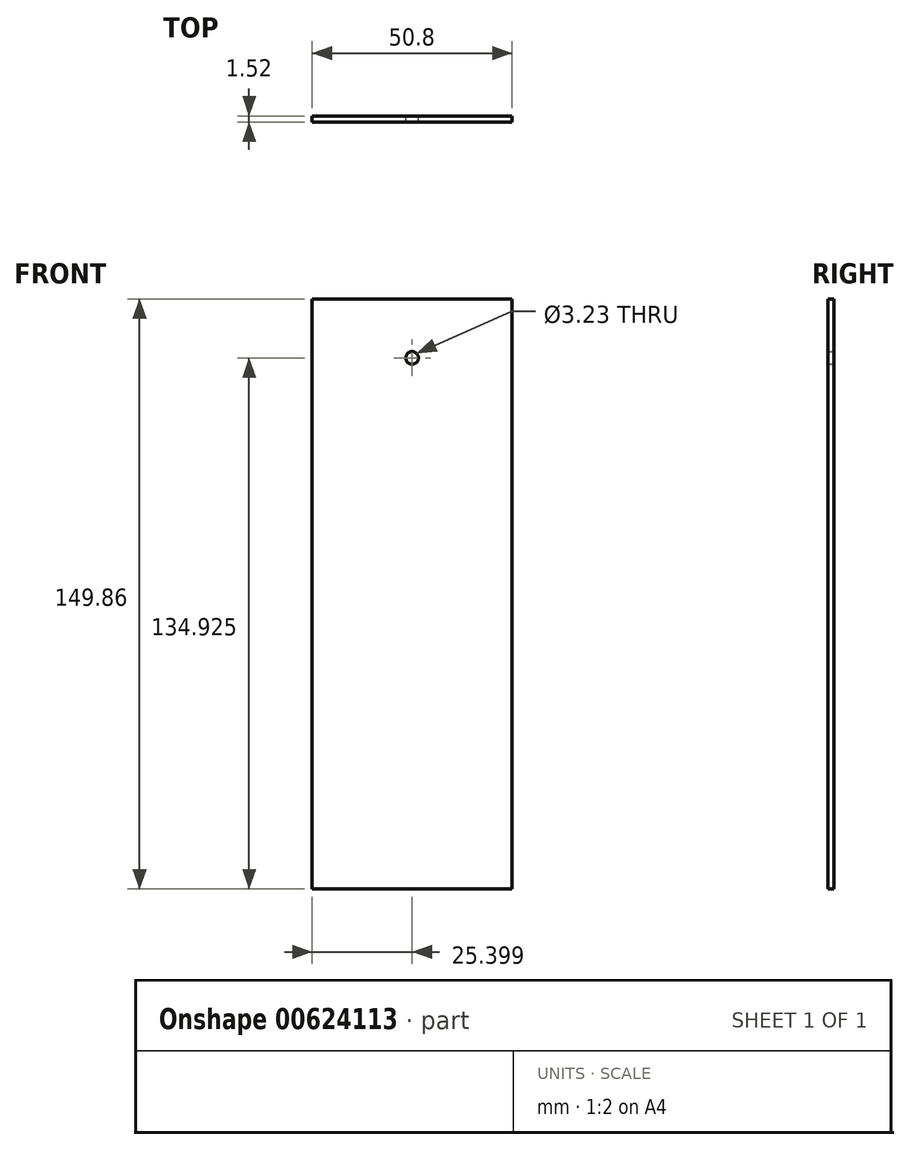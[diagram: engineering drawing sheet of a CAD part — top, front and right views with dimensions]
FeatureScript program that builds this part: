
annotation { "Feature Type Name" : "Feature", "Feature Type Description" : "" }
export const myFeature = defineFeature(function(context is Context, id is Id, definition is map)
    precondition{}
    {
        {
            var Q0;
            Q0=qCreatedBy(makeId("Front.planeOp"),FACE);
            var sketch = newSketch(context, id + "F0", { "sketchPlane" : qUnion([Q0])});
            skLineSegment(sketch, "E0.bottom", {"start": v(-102.41, 87.01) * mm, "end": v(-51.61, 87.01) * mm});
            skLineSegment(sketch, "E0.top", {"start": v(-102.41, -62.85) * mm, "end": v(-51.61, -62.85) * mm});
            skLineSegment(sketch, "E0.left", {"start": v(-102.41, 87.01) * mm, "end": v(-102.41, -62.85) * mm});
            skLineSegment(sketch, "E0.right", {"start": v(-51.61, 87.01) * mm, "end": v(-51.61, -62.85) * mm});
            skCircle(sketch, "E1", {"center": v(-77.01, 72.08) * mm, "radius": 1.61 * mm});
            skPoint(sketch, "E1.centerSnap0", {"position": v(-77.01, 87.01) * mm});
            skSolve(sketch);
        }
        {
            var Q0;
            Q0 = qSketchRegion(id + "F0", true);
            extrude(context, id + "F1", {"entities" : qUnion([Q0]), "endBound" : BoundingType.SYMMETRIC, "depth" : 1.52 * mm, "offsetDistance" : 25.4 * mm});
        }
    });
